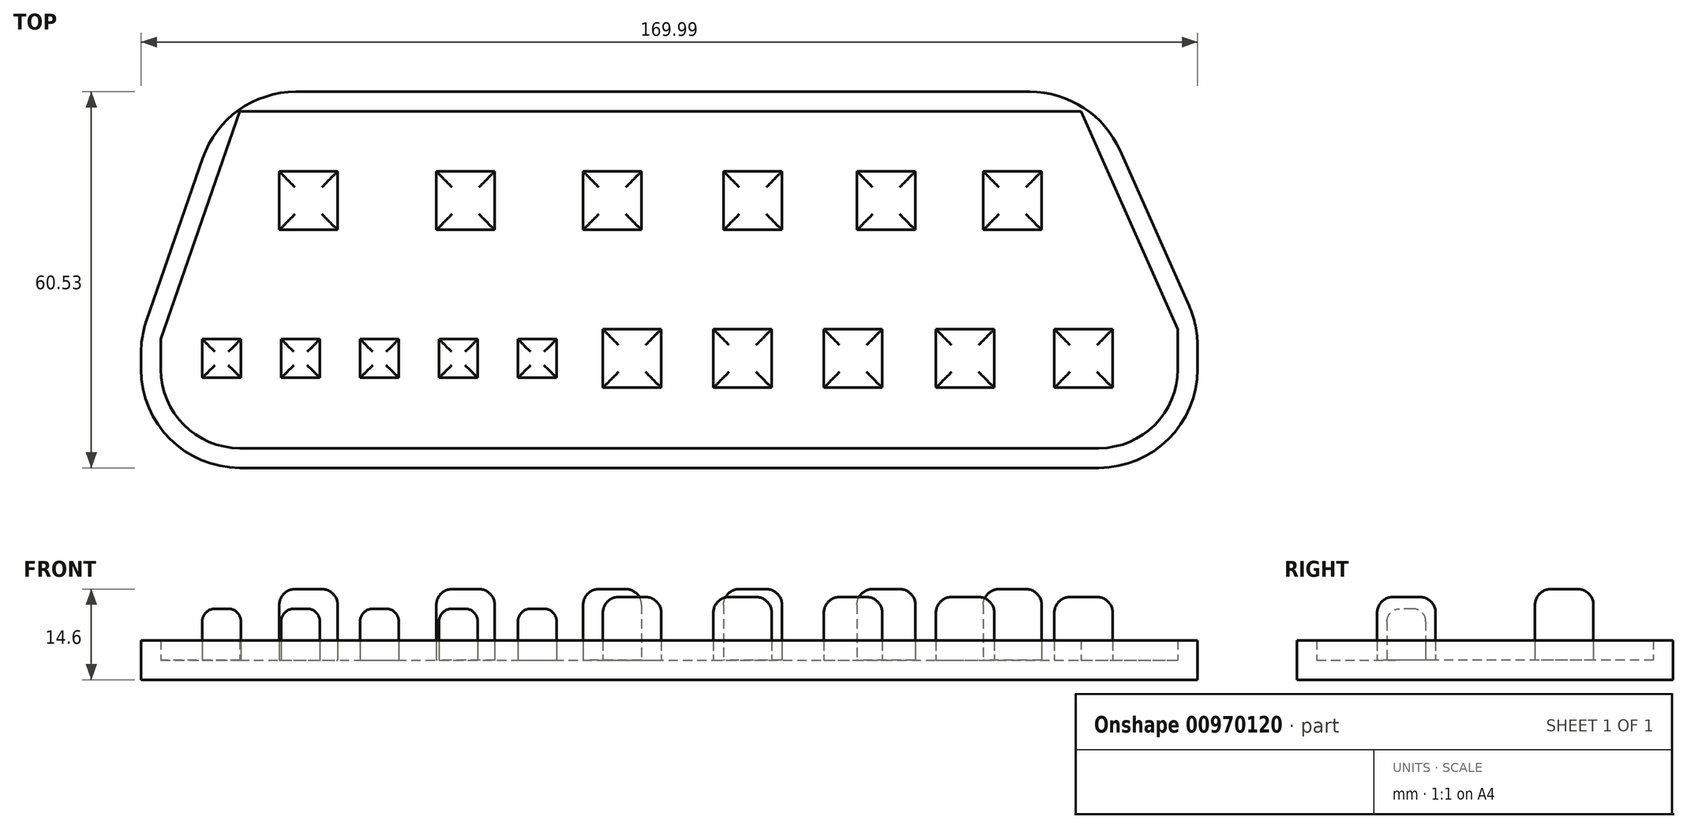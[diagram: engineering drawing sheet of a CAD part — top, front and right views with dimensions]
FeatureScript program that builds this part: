
annotation { "Feature Type Name" : "Feature", "Feature Type Description" : "" }
export const myFeature = defineFeature(function(context is Context, id is Id, definition is map)
    precondition{}
    {
        {
            var Q0;
            Q0=qCreatedBy(makeId("Top.planeOp"),FACE);
            var sketch = newSketch(context, id + "F0", { "sketchPlane" : qUnion([Q0])});
            skLineSegment(sketch, "E0.bottom", {"start": v(-9.72, 0.4) * mm, "end": v(153.92, 0.4) * mm});
            skLineSegment(sketch, "E0.top", {"start": v(-9.72, -53.77) * mm, "end": v(153.92, -53.77) * mm});
            skLineSegment(sketch, "E0.left", {"start": v(-9.72, 0.4) * mm, "end": v(-9.72, -53.77) * mm});
            skLineSegment(sketch, "E0.right", {"start": v(153.92, 0.4) * mm, "end": v(153.92, -53.77) * mm});
            skSolve(sketch);
        }
        {
            var Q0;
            Q0=makeQuery(id+"F0.imprint","IMPRINT",FACE,{"disambiguationData":[TD([[makeQuery(id+"F0.imprint","IMPRINT",EDGE,{"derivedFrom":sQuery(id+"F0.wireOp",EDGE,"E0.bottom")}),-1.0]])]});
            extrude(context, id + "F1", {"entities" : qUnion([Q0]), "oppositeDirection" : true, "depth" : 3.17 * mm, "offsetDistance" : 25.4 * mm});
        }
        {
            var Q0;
            Q0=qCreatedBy(makeId("Top.planeOp"),FACE);
            var sketch = newSketch(context, id + "F2", { "sketchPlane" : qUnion([Q0])});
            skLineSegment(sketch, "E1.bottom", {"start": v(9.33, -9.25) * mm, "end": v(18.73, -9.25) * mm});
            skLineSegment(sketch, "E1.top", {"start": v(9.33, -18.64) * mm, "end": v(18.73, -18.64) * mm});
            skLineSegment(sketch, "E1.left", {"start": v(9.33, -9.25) * mm, "end": v(9.33, -18.64) * mm});
            skLineSegment(sketch, "E1.right", {"start": v(18.73, -9.25) * mm, "end": v(18.73, -18.64) * mm});
            skLineSegment(sketch, "E2.bottom", {"start": v(44, -9.25) * mm, "end": v(34.6, -9.25) * mm});
            skLineSegment(sketch, "E2.top", {"start": v(44, -18.64) * mm, "end": v(34.6, -18.64) * mm});
            skLineSegment(sketch, "E2.left", {"start": v(44, -9.25) * mm, "end": v(44, -18.64) * mm});
            skLineSegment(sketch, "E3.bottom", {"start": v(67.63, -9.25) * mm, "end": v(58.23, -9.25) * mm});
            skLineSegment(sketch, "E3.top", {"start": v(67.63, -18.64) * mm, "end": v(58.23, -18.64) * mm});
            skLineSegment(sketch, "E3.left", {"start": v(67.63, -9.25) * mm, "end": v(67.63, -18.64) * mm});
            skLineSegment(sketch, "E3.right", {"start": v(58.23, -9.25) * mm, "end": v(58.23, -18.64) * mm});
            skLineSegment(sketch, "E4.bottom", {"start": v(90.23, -9.25) * mm, "end": v(80.84, -9.25) * mm});
            skLineSegment(sketch, "E4.top", {"start": v(90.23, -18.64) * mm, "end": v(80.84, -18.64) * mm});
            skLineSegment(sketch, "E4.left", {"start": v(90.23, -9.25) * mm, "end": v(90.23, -18.64) * mm});
            skLineSegment(sketch, "E4.right", {"start": v(80.84, -9.25) * mm, "end": v(80.84, -18.64) * mm});
            skLineSegment(sketch, "E5.bottom", {"start": v(111.7, -9.25) * mm, "end": v(102.3, -9.25) * mm});
            skLineSegment(sketch, "E5.top", {"start": v(111.7, -18.64) * mm, "end": v(102.3, -18.64) * mm});
            skLineSegment(sketch, "E5.left", {"start": v(111.7, -9.25) * mm, "end": v(111.7, -18.64) * mm});
            skLineSegment(sketch, "E5.right", {"start": v(102.3, -9.25) * mm, "end": v(102.3, -18.64) * mm});
            skLineSegment(sketch, "E6.bottom", {"start": v(132.02, -9.25) * mm, "end": v(122.62, -9.25) * mm});
            skLineSegment(sketch, "E6.top", {"start": v(132.02, -18.64) * mm, "end": v(122.62, -18.64) * mm});
            skLineSegment(sketch, "E6.left", {"start": v(132.02, -9.25) * mm, "end": v(132.02, -18.64) * mm});
            skLineSegment(sketch, "E6.right", {"start": v(122.62, -9.25) * mm, "end": v(122.62, -18.64) * mm});
            skLineSegment(sketch, "E7", {"start": v(34.6, -9.25) * mm, "end": v(34.6, -18.64) * mm});
            skSolve(sketch);
        }
        {
            var Q0;
            Q0=makeQuery(id+"F2.imprint","IMPRINT",FACE,{"disambiguationData":[TD([[makeQuery(id+"F2.imprint","IMPRINT",EDGE,{"derivedFrom":sQuery(id+"F2.wireOp",EDGE,"E1.bottom")}),-1.0]])]});
            var Q1;
            Q1=makeQuery(id+"F2.imprint","IMPRINT",FACE,{"disambiguationData":[TD([[makeQuery(id+"F2.imprint","IMPRINT",EDGE,{"derivedFrom":sQuery(id+"F2.wireOp",EDGE,"E2.bottom")}),1.0]])]});
            var Q2;
            Q2=makeQuery(id+"F2.imprint","IMPRINT",FACE,{"disambiguationData":[TD([[makeQuery(id+"F2.imprint","IMPRINT",EDGE,{"derivedFrom":sQuery(id+"F2.wireOp",EDGE,"E3.bottom")}),1.0]])]});
            var Q3;
            Q3=makeQuery(id+"F2.imprint","IMPRINT",FACE,{"disambiguationData":[TD([[makeQuery(id+"F2.imprint","IMPRINT",EDGE,{"derivedFrom":sQuery(id+"F2.wireOp",EDGE,"E4.bottom")}),1.0]])]});
            var Q4;
            Q4=makeQuery(id+"F2.imprint","IMPRINT",FACE,{"disambiguationData":[TD([[makeQuery(id+"F2.imprint","IMPRINT",EDGE,{"derivedFrom":sQuery(id+"F2.wireOp",EDGE,"E5.bottom")}),1.0]])]});
            var Q5;
            Q5=makeQuery(id+"F2.imprint","IMPRINT",FACE,{"disambiguationData":[TD([[makeQuery(id+"F2.imprint","IMPRINT",EDGE,{"derivedFrom":sQuery(id+"F2.wireOp",EDGE,"E6.bottom")}),1.0]])]});
            extrude(context, id + "F3", {"entities" : qUnion([Q0, Q1, Q2, Q3, Q4, Q5]), "operationType" : NewBodyOperationType.ADD, "depth" : 11.43 * mm, "offsetDistance" : 25.4 * mm});
        }
        {
            var Q0;
            Q0=makeQuery(id+"F1.opExtrude","CAP_FACE",FACE,{"disambiguationData":[OSD([sQuery(id+"F0.wireOp",EDGE,"E0.bottom"),sQuery(id+"F0.wireOp",EDGE,"E0.top"),sQuery(id+"F0.wireOp",EDGE,"E0.left"),sQuery(id+"F0.wireOp",EDGE,"E0.right")])],"isStart":true});
            var sketch = newSketch(context, id + "F4", { "sketchPlane" : qUnion([Q0])});
            skLineSegment(sketch, "E8", {"start": v(61.4, -34.65) * mm, "end": v(193.08, -34.65) * mm, "construction": true});
            skLineSegment(sketch, "E9.bottom", {"start": v(61.4, -34.65) * mm, "end": v(70.8, -34.65) * mm});
            skLineSegment(sketch, "E9.top", {"start": v(61.4, -44.04) * mm, "end": v(70.8, -44.04) * mm});
            skLineSegment(sketch, "E9.left", {"start": v(61.4, -34.65) * mm, "end": v(61.4, -44.04) * mm});
            skLineSegment(sketch, "E9.right", {"start": v(70.8, -34.65) * mm, "end": v(70.8, -44.04) * mm});
            skLineSegment(sketch, "E10.bottom", {"start": v(79.18, -34.65) * mm, "end": v(88.58, -34.65) * mm});
            skLineSegment(sketch, "E10.top", {"start": v(79.18, -44.04) * mm, "end": v(88.58, -44.04) * mm});
            skLineSegment(sketch, "E10.left", {"start": v(79.18, -34.65) * mm, "end": v(79.18, -44.04) * mm});
            skLineSegment(sketch, "E10.right", {"start": v(88.58, -34.65) * mm, "end": v(88.58, -44.04) * mm});
            skLineSegment(sketch, "E11.bottom", {"start": v(96.96, -34.65) * mm, "end": v(106.36, -34.65) * mm});
            skLineSegment(sketch, "E11.top", {"start": v(96.96, -44.04) * mm, "end": v(106.36, -44.04) * mm});
            skLineSegment(sketch, "E11.left", {"start": v(96.96, -34.65) * mm, "end": v(96.96, -44.04) * mm});
            skLineSegment(sketch, "E11.right", {"start": v(106.36, -34.65) * mm, "end": v(106.36, -44.04) * mm});
            skLineSegment(sketch, "E12.bottom", {"start": v(115, -34.65) * mm, "end": v(124.4, -34.65) * mm});
            skLineSegment(sketch, "E12.top", {"start": v(115, -44.04) * mm, "end": v(124.4, -44.04) * mm});
            skLineSegment(sketch, "E12.left", {"start": v(115, -34.65) * mm, "end": v(115, -44.04) * mm});
            skLineSegment(sketch, "E12.right", {"start": v(124.4, -34.65) * mm, "end": v(124.4, -44.04) * mm});
            skLineSegment(sketch, "E13.bottom", {"start": v(134.05, -34.65) * mm, "end": v(143.45, -34.65) * mm});
            skLineSegment(sketch, "E13.top", {"start": v(134.05, -44.04) * mm, "end": v(143.45, -44.04) * mm});
            skLineSegment(sketch, "E13.left", {"start": v(134.05, -34.65) * mm, "end": v(134.05, -44.04) * mm});
            skLineSegment(sketch, "E13.right", {"start": v(143.45, -34.65) * mm, "end": v(143.45, -44.04) * mm});
            skSolve(sketch);
        }
        {
            var Q0;
            Q0=makeQuery(id+"F4.imprint","IMPRINT",FACE,{"disambiguationData":[TD([[makeQuery(id+"F4.imprint","IMPRINT",EDGE,{"derivedFrom":sQuery(id+"F4.wireOp",EDGE,"E11.bottom")}),-1.0]])]});
            var Q1;
            Q1=makeQuery(id+"F4.imprint","IMPRINT",FACE,{"disambiguationData":[TD([[makeQuery(id+"F4.imprint","IMPRINT",EDGE,{"derivedFrom":sQuery(id+"F4.wireOp",EDGE,"E13.bottom")}),-1.0]])]});
            var Q2;
            Q2=makeQuery(id+"F4.imprint","IMPRINT",FACE,{"disambiguationData":[TD([[makeQuery(id+"F4.imprint","IMPRINT",EDGE,{"derivedFrom":sQuery(id+"F4.wireOp",EDGE,"E12.bottom")}),-1.0]])]});
            var Q3;
            Q3=makeQuery(id+"F4.imprint","IMPRINT",FACE,{"disambiguationData":[TD([[makeQuery(id+"F4.imprint","IMPRINT",EDGE,{"derivedFrom":sQuery(id+"F4.wireOp",EDGE,"E10.bottom")}),-1.0]])]});
            var Q4;
            Q4=makeQuery(id+"F4.imprint","IMPRINT",FACE,{"disambiguationData":[TD([[makeQuery(id+"F4.imprint","IMPRINT",EDGE,{"derivedFrom":sQuery(id+"F4.wireOp",EDGE,"E9.bottom")}),-1.0]])]});
            extrude(context, id + "F5", {"entities" : qUnion([Q0, Q1, Q2, Q3, Q4]), "operationType" : NewBodyOperationType.ADD, "depth" : 10.16 * mm, "offsetDistance" : 25.4 * mm});
        }
        {
            var Q0;
            Q0=makeQuery(id+"F3.opExtrude","CAP_FACE",FACE,{"disambiguationData":[OSD([sQuery(id+"F2.wireOp",EDGE,"E1.bottom"),sQuery(id+"F2.wireOp",EDGE,"E1.top"),sQuery(id+"F2.wireOp",EDGE,"E1.left"),sQuery(id+"F2.wireOp",EDGE,"E1.right")])],"isStart":false});
            var Q1;
            Q1=makeQuery(id+"F3.opExtrude","CAP_FACE",FACE,{"disambiguationData":[OSD([sQuery(id+"F2.wireOp",EDGE,"a6f74513-a6f5-46e5-be97-dc0fd28510d1.1.0.0"),sQuery(id+"F2.wireOp",EDGE,"a6f74513-a6f5-46e5-be97-dc0fd28510d1.1.0.1"),sQuery(id+"F2.wireOp",EDGE,"a6f74513-a6f5-46e5-be97-dc0fd28510d1.1.0.2"),sQuery(id+"F2.wireOp",EDGE,"a6f74513-a6f5-46e5-be97-dc0fd28510d1.1.0.3")])],"isStart":false});
            var Q2;
            Q2=makeQuery(id+"F3.opExtrude","CAP_FACE",FACE,{"disambiguationData":[OSD([sQuery(id+"F2.wireOp",EDGE,"a37b4573-0c43-4b9e-b34a-351aa36ba832.1.0.0"),sQuery(id+"F2.wireOp",EDGE,"a37b4573-0c43-4b9e-b34a-351aa36ba832.1.0.1"),sQuery(id+"F2.wireOp",EDGE,"a37b4573-0c43-4b9e-b34a-351aa36ba832.1.0.2"),sQuery(id+"F2.wireOp",EDGE,"a37b4573-0c43-4b9e-b34a-351aa36ba832.1.0.3")])],"isStart":false});
            var Q3;
            Q3=makeQuery(id+"F3.opExtrude","CAP_FACE",FACE,{"disambiguationData":[OSD([sQuery(id+"F2.wireOp",EDGE,"2544778d-07a4-4a01-85e0-11865cb4e7f5.1.0.0"),sQuery(id+"F2.wireOp",EDGE,"2544778d-07a4-4a01-85e0-11865cb4e7f5.1.0.2"),sQuery(id+"F2.wireOp",EDGE,"2544778d-07a4-4a01-85e0-11865cb4e7f5.1.0.3"),sQuery(id+"F2.wireOp",EDGE,"2544778d-07a4-4a01-85e0-11865cb4e7f5.1.0.4")])],"isStart":false});
            var Q4;
            Q4=makeQuery(id+"F3.opExtrude","CAP_FACE",FACE,{"disambiguationData":[OSD([sQuery(id+"F2.wireOp",EDGE,"e6729a68-15cc-43d3-9dee-f7c0bf543b0e.1.0.0"),sQuery(id+"F2.wireOp",EDGE,"e6729a68-15cc-43d3-9dee-f7c0bf543b0e.1.0.1"),sQuery(id+"F2.wireOp",EDGE,"e6729a68-15cc-43d3-9dee-f7c0bf543b0e.1.0.2"),sQuery(id+"F2.wireOp",EDGE,"e6729a68-15cc-43d3-9dee-f7c0bf543b0e.1.0.3")])],"isStart":false});
            var Q5;
            Q5=makeQuery(id+"F3.opExtrude","CAP_FACE",FACE,{"disambiguationData":[OSD([sQuery(id+"F2.wireOp",EDGE,"b651a250-4a59-4ffa-a352-21a7c59f4deb.1.0.0"),sQuery(id+"F2.wireOp",EDGE,"b651a250-4a59-4ffa-a352-21a7c59f4deb.1.0.1"),sQuery(id+"F2.wireOp",EDGE,"b651a250-4a59-4ffa-a352-21a7c59f4deb.1.0.2"),sQuery(id+"F2.wireOp",EDGE,"b651a250-4a59-4ffa-a352-21a7c59f4deb.1.0.3")])],"isStart":false});
            var Q6;
            Q6=makeQuery(id+"F3.opExtrude","CAP_FACE",FACE,{"disambiguationData":[OSD([sQuery(id+"F2.wireOp",EDGE,"60ef9c8b-74d5-4385-bd4f-73c425923557.1.0.0"),sQuery(id+"F2.wireOp",EDGE,"60ef9c8b-74d5-4385-bd4f-73c425923557.1.0.1"),sQuery(id+"F2.wireOp",EDGE,"60ef9c8b-74d5-4385-bd4f-73c425923557.1.0.2"),sQuery(id+"F2.wireOp",EDGE,"60ef9c8b-74d5-4385-bd4f-73c425923557.1.0.3")])],"isStart":false});
            var Q7;
            Q7=makeQuery(id+"F3.opExtrude","CAP_FACE",FACE,{"disambiguationData":[OSD([sQuery(id+"F2.wireOp",EDGE,"5298001d-e36e-4064-a5db-c45dce80e3df.1.0.1"),sQuery(id+"F2.wireOp",EDGE,"5298001d-e36e-4064-a5db-c45dce80e3df.1.0.2"),sQuery(id+"F2.wireOp",EDGE,"5298001d-e36e-4064-a5db-c45dce80e3df.1.0.3"),sQuery(id+"F2.wireOp",EDGE,"5298001d-e36e-4064-a5db-c45dce80e3df.1.0.4")])],"isStart":false});
            var Q8;
            Q8=makeQuery(id+"F3.opExtrude","CAP_FACE",FACE,{"disambiguationData":[OSD([sQuery(id+"F2.wireOp",EDGE,"E2.bottom"),sQuery(id+"F2.wireOp",EDGE,"E2.top"),sQuery(id+"F2.wireOp",EDGE,"E2.left"),sQuery(id+"F2.wireOp",EDGE,"E2.right")])],"isStart":false});
            var Q9;
            Q9=makeQuery(id+"F3.opExtrude","CAP_FACE",FACE,{"disambiguationData":[OSD([sQuery(id+"F2.wireOp",EDGE,"E3.bottom"),sQuery(id+"F2.wireOp",EDGE,"E3.top"),sQuery(id+"F2.wireOp",EDGE,"E3.left"),sQuery(id+"F2.wireOp",EDGE,"E3.right")])],"isStart":false});
            var Q10;
            Q10=makeQuery(id+"F3.opExtrude","CAP_FACE",FACE,{"disambiguationData":[OSD([sQuery(id+"F2.wireOp",EDGE,"E4.bottom"),sQuery(id+"F2.wireOp",EDGE,"E4.top"),sQuery(id+"F2.wireOp",EDGE,"E4.left"),sQuery(id+"F2.wireOp",EDGE,"E4.right")])],"isStart":false});
            var Q11;
            Q11=makeQuery(id+"F3.opExtrude","CAP_FACE",FACE,{"disambiguationData":[OSD([sQuery(id+"F2.wireOp",EDGE,"E5.bottom"),sQuery(id+"F2.wireOp",EDGE,"E5.top"),sQuery(id+"F2.wireOp",EDGE,"E5.left"),sQuery(id+"F2.wireOp",EDGE,"E5.right")])],"isStart":false});
            var Q12;
            Q12=makeQuery(id+"F3.opExtrude","CAP_FACE",FACE,{"disambiguationData":[OSD([sQuery(id+"F2.wireOp",EDGE,"E6.bottom"),sQuery(id+"F2.wireOp",EDGE,"E6.top"),sQuery(id+"F2.wireOp",EDGE,"E6.left"),sQuery(id+"F2.wireOp",EDGE,"E6.right")])],"isStart":false});
            fillet(context, id + "F6", {"entities" : qUnion([Q0, Q1, Q2, Q3, Q4, Q5, Q6, Q7, Q8, Q9, Q10, Q11, Q12]), "radius" : 2.54 * mm, "tangentPropagation" : true, "allowEdgeOverflow" : false});
        }
        {
            var Q0;
            Q0=makeQuery(id+"F5.opExtrude","CAP_FACE",FACE,{"disambiguationData":[OSD([sQuery(id+"F4.wireOp",EDGE,"E9.bottom"),sQuery(id+"F4.wireOp",EDGE,"E9.top"),sQuery(id+"F4.wireOp",EDGE,"E9.left"),sQuery(id+"F4.wireOp",EDGE,"E9.right")])],"isStart":false});
            var Q1;
            Q1=makeQuery(id+"F5.opExtrude","CAP_FACE",FACE,{"disambiguationData":[OSD([sQuery(id+"F4.wireOp",EDGE,"E10.bottom"),sQuery(id+"F4.wireOp",EDGE,"E10.top"),sQuery(id+"F4.wireOp",EDGE,"E10.left"),sQuery(id+"F4.wireOp",EDGE,"E10.right")])],"isStart":false});
            var Q2;
            Q2=makeQuery(id+"F5.opExtrude","CAP_FACE",FACE,{"disambiguationData":[OSD([sQuery(id+"F4.wireOp",EDGE,"E11.bottom"),sQuery(id+"F4.wireOp",EDGE,"E11.top"),sQuery(id+"F4.wireOp",EDGE,"E11.left"),sQuery(id+"F4.wireOp",EDGE,"E11.right")])],"isStart":false});
            var Q3;
            Q3=makeQuery(id+"F5.opExtrude","CAP_FACE",FACE,{"disambiguationData":[OSD([sQuery(id+"F4.wireOp",EDGE,"E12.bottom"),sQuery(id+"F4.wireOp",EDGE,"E12.top"),sQuery(id+"F4.wireOp",EDGE,"E12.left"),sQuery(id+"F4.wireOp",EDGE,"E12.right")])],"isStart":false});
            var Q4;
            Q4=makeQuery(id+"F5.opExtrude","CAP_FACE",FACE,{"disambiguationData":[OSD([sQuery(id+"F4.wireOp",EDGE,"E13.bottom"),sQuery(id+"F4.wireOp",EDGE,"E13.top"),sQuery(id+"F4.wireOp",EDGE,"E13.left"),sQuery(id+"F4.wireOp",EDGE,"E13.right")])],"isStart":false});
            var Q5;
            Q5=makeQuery(id+"F5.opExtrude","CAP_FACE",FACE,{"disambiguationData":[OSD([sQuery(id+"F4.wireOp",EDGE,"HuPphu0x-Gtiq-LhBo-5UTa-TvdvrvVJAFvw.bottom"),sQuery(id+"F4.wireOp",EDGE,"HuPphu0x-Gtiq-LhBo-5UTa-TvdvrvVJAFvw.top"),sQuery(id+"F4.wireOp",EDGE,"HuPphu0x-Gtiq-LhBo-5UTa-TvdvrvVJAFvw.left"),sQuery(id+"F4.wireOp",EDGE,"HuPphu0x-Gtiq-LhBo-5UTa-TvdvrvVJAFvw.right")])],"isStart":false});
            var Q6;
            Q6=makeQuery(id+"F5.opExtrude","CAP_FACE",FACE,{"disambiguationData":[OSD([sQuery(id+"F4.wireOp",EDGE,"e8lRvLqR-yIOs-Yckj-3nDI-QBPCZNJgAbyx.bottom"),sQuery(id+"F4.wireOp",EDGE,"e8lRvLqR-yIOs-Yckj-3nDI-QBPCZNJgAbyx.top"),sQuery(id+"F4.wireOp",EDGE,"e8lRvLqR-yIOs-Yckj-3nDI-QBPCZNJgAbyx.left"),sQuery(id+"F4.wireOp",EDGE,"e8lRvLqR-yIOs-Yckj-3nDI-QBPCZNJgAbyx.right")])],"isStart":false});
            var Q7;
            Q7=makeQuery(id+"F5.opExtrude","CAP_FACE",FACE,{"disambiguationData":[OSD([sQuery(id+"F4.wireOp",EDGE,"93dc5489-29b0-42f7-b222-2c44c2208c07.1.0.0"),sQuery(id+"F4.wireOp",EDGE,"93dc5489-29b0-42f7-b222-2c44c2208c07.1.0.1"),sQuery(id+"F4.wireOp",EDGE,"93dc5489-29b0-42f7-b222-2c44c2208c07.1.0.2"),sQuery(id+"F4.wireOp",EDGE,"93dc5489-29b0-42f7-b222-2c44c2208c07.1.0.3")])],"isStart":false});
            fillet(context, id + "F7", {"entities" : qUnion([Q0, Q1, Q2, Q3, Q4, Q5, Q6, Q7]), "radius" : 2.54 * mm, "tangentPropagation" : true, "allowEdgeOverflow" : false});
        }
        {
            var Q0;
            Q0=makeQuery(id+"F1.opExtrude","CAP_FACE",FACE,{"disambiguationData":[OSD([sQuery(id+"F0.wireOp",EDGE,"E0.bottom"),sQuery(id+"F0.wireOp",EDGE,"E0.top"),sQuery(id+"F0.wireOp",EDGE,"E0.left"),sQuery(id+"F0.wireOp",EDGE,"E0.right")])],"isStart":true});
            var sketch = newSketch(context, id + "F8", { "sketchPlane" : qUnion([Q0])});
            skLineSegment(sketch, "E14", {"start": v(113.95, -36.23) * mm, "end": v(235.74, -36.23) * mm, "construction": true});
            skLineSegment(sketch, "E15.bottom", {"start": v(47.75, -36.23) * mm, "end": v(53.98, -36.23) * mm});
            skLineSegment(sketch, "E15.top", {"start": v(47.75, -42.46) * mm, "end": v(53.98, -42.46) * mm});
            skLineSegment(sketch, "E15.left", {"start": v(47.75, -36.23) * mm, "end": v(47.75, -42.46) * mm});
            skLineSegment(sketch, "E15.right", {"start": v(53.98, -36.23) * mm, "end": v(53.98, -42.46) * mm});
            skLineSegment(sketch, "E16.1.0.0", {"start": v(41.28, -36.23) * mm, "end": v(41.28, -42.46) * mm});
            skLineSegment(sketch, "E16.1.0.1", {"start": v(35.05, -36.23) * mm, "end": v(41.28, -36.23) * mm});
            skLineSegment(sketch, "E16.1.0.2", {"start": v(35.05, -36.23) * mm, "end": v(35.05, -42.46) * mm});
            skLineSegment(sketch, "E16.1.0.3", {"start": v(35.05, -42.46) * mm, "end": v(41.28, -42.46) * mm});
            skLineSegment(sketch, "E16.2.0.0", {"start": v(28.58, -36.23) * mm, "end": v(28.58, -42.46) * mm});
            skLineSegment(sketch, "E16.2.0.1", {"start": v(22.35, -36.23) * mm, "end": v(28.58, -36.23) * mm});
            skLineSegment(sketch, "E16.2.0.2", {"start": v(22.35, -36.23) * mm, "end": v(22.35, -42.46) * mm});
            skLineSegment(sketch, "E16.2.0.3", {"start": v(22.35, -42.46) * mm, "end": v(28.58, -42.46) * mm});
            skLineSegment(sketch, "E16.3.0.0", {"start": v(15.88, -36.23) * mm, "end": v(15.88, -42.46) * mm});
            skLineSegment(sketch, "E16.3.0.1", {"start": v(9.65, -36.23) * mm, "end": v(15.88, -36.23) * mm});
            skLineSegment(sketch, "E16.3.0.2", {"start": v(9.65, -36.23) * mm, "end": v(9.65, -42.46) * mm});
            skLineSegment(sketch, "E16.3.0.3", {"start": v(9.65, -42.46) * mm, "end": v(15.88, -42.46) * mm});
            skLineSegment(sketch, "E16.4.0.0", {"start": v(3.17, -36.23) * mm, "end": v(3.17, -42.46) * mm});
            skLineSegment(sketch, "E16.4.0.1", {"start": v(-3.05, -36.23) * mm, "end": v(3.17, -36.23) * mm});
            skLineSegment(sketch, "E16.4.0.2", {"start": v(-3.05, -36.23) * mm, "end": v(-3.05, -42.46) * mm});
            skLineSegment(sketch, "E16.4.0.3", {"start": v(-3.05, -42.46) * mm, "end": v(3.17, -42.46) * mm});
            skLineSegment(sketch, "E16.direction1", {"start": v(47.75, -42.46) * mm, "end": v(35.05, -42.46) * mm, "construction": true});
            skSolve(sketch);
        }
        {
            var Q0;
            Q0=makeQuery(id+"F8.imprint","IMPRINT",FACE,{"disambiguationData":[TD([[makeQuery(id+"F8.imprint","IMPRINT",EDGE,{"derivedFrom":sQuery(id+"F8.wireOp",EDGE,"E15.bottom")}),-1.0]])]});
            var Q1;
            Q1=makeQuery(id+"F8.imprint","IMPRINT",FACE,{"disambiguationData":[TD([[makeQuery(id+"F8.imprint","IMPRINT",EDGE,{"derivedFrom":sQuery(id+"F8.wireOp",EDGE,"E16.1.0.0")}),-1.0]])]});
            var Q2;
            Q2=makeQuery(id+"F8.imprint","IMPRINT",FACE,{"disambiguationData":[TD([[makeQuery(id+"F8.imprint","IMPRINT",EDGE,{"derivedFrom":sQuery(id+"F8.wireOp",EDGE,"E16.2.0.0")}),-1.0]])]});
            var Q3;
            Q3=makeQuery(id+"F8.imprint","IMPRINT",FACE,{"disambiguationData":[TD([[makeQuery(id+"F8.imprint","IMPRINT",EDGE,{"derivedFrom":sQuery(id+"F8.wireOp",EDGE,"E16.3.0.0")}),-1.0]])]});
            var Q4;
            Q4=makeQuery(id+"F8.imprint","IMPRINT",FACE,{"disambiguationData":[TD([[makeQuery(id+"F8.imprint","IMPRINT",EDGE,{"derivedFrom":sQuery(id+"F8.wireOp",EDGE,"E16.4.0.0")}),-1.0]])]});
            var Q5;
            Q5=sQuery(id+"F8.wireOp",EDGE,"A3gFyePg-5LmW-fe9U-Uoda-R7NkxVjHE0qn.left");
            var Q6;
            Q6=sQuery(id+"F8.wireOp",EDGE,"A3gFyePg-5LmW-fe9U-Uoda-R7NkxVjHE0qn.bottom");
            var Q7;
            Q7=sQuery(id+"F8.wireOp",EDGE,"A3gFyePg-5LmW-fe9U-Uoda-R7NkxVjHE0qn.right");
            var Q8;
            Q8=sQuery(id+"F8.wireOp",EDGE,"A3gFyePg-5LmW-fe9U-Uoda-R7NkxVjHE0qn.top");
            extrude(context, id + "F9", {"entities" : qUnion([Q0, Q1, Q2, Q3, Q4]), "operationType" : NewBodyOperationType.ADD, "surfaceEntities" : qUnion([Q5, Q6, Q7, Q8]), "depth" : 8.25 * mm, "offsetDistance" : 25.4 * mm});
        }
        {
            var Q0;
            Q0=makeQuery(id+"F9.opExtrude","CAP_FACE",FACE,{"disambiguationData":[OSD([sQuery(id+"F8.wireOp",EDGE,"E15.bottom"),sQuery(id+"F8.wireOp",EDGE,"E15.top"),sQuery(id+"F8.wireOp",EDGE,"E15.left"),sQuery(id+"F8.wireOp",EDGE,"E15.right")])],"isStart":false});
            var Q1;
            Q1=makeQuery(id+"F9.opExtrude","CAP_FACE",FACE,{"disambiguationData":[OSD([sQuery(id+"F8.wireOp",EDGE,"E16.1.0.0"),sQuery(id+"F8.wireOp",EDGE,"E16.1.0.1"),sQuery(id+"F8.wireOp",EDGE,"E16.1.0.2"),sQuery(id+"F8.wireOp",EDGE,"E16.1.0.3")])],"isStart":false});
            var Q2;
            Q2=makeQuery(id+"F9.opExtrude","CAP_FACE",FACE,{"disambiguationData":[OSD([sQuery(id+"F8.wireOp",EDGE,"E16.2.0.0"),sQuery(id+"F8.wireOp",EDGE,"E16.2.0.1"),sQuery(id+"F8.wireOp",EDGE,"E16.2.0.2"),sQuery(id+"F8.wireOp",EDGE,"E16.2.0.3")])],"isStart":false});
            var Q3;
            Q3=makeQuery(id+"F9.opExtrude","CAP_FACE",FACE,{"disambiguationData":[OSD([sQuery(id+"F8.wireOp",EDGE,"E16.3.0.0"),sQuery(id+"F8.wireOp",EDGE,"E16.3.0.1"),sQuery(id+"F8.wireOp",EDGE,"E16.3.0.2"),sQuery(id+"F8.wireOp",EDGE,"E16.3.0.3")])],"isStart":false});
            var Q4;
            Q4=makeQuery(id+"F9.opExtrude","CAP_FACE",FACE,{"disambiguationData":[OSD([sQuery(id+"F8.wireOp",EDGE,"E16.4.0.0"),sQuery(id+"F8.wireOp",EDGE,"E16.4.0.1"),sQuery(id+"F8.wireOp",EDGE,"E16.4.0.2"),sQuery(id+"F8.wireOp",EDGE,"E16.4.0.3")])],"isStart":false});
            fillet(context, id + "F10", {"entities" : qUnion([Q0, Q1, Q2, Q3, Q4]), "radius" : 2.03 * mm, "tangentPropagation" : true, "allowEdgeOverflow" : false});
        }
        {
            var Q0;
            Q0=makeQuery(id+"F1.opExtrude","CAP_FACE",FACE,{"disambiguationData":[OSD([sQuery(id+"F0.wireOp",EDGE,"E0.bottom"),sQuery(id+"F0.wireOp",EDGE,"E0.top"),sQuery(id+"F0.wireOp",EDGE,"E0.left"),sQuery(id+"F0.wireOp",EDGE,"E0.right")])],"isStart":true});
            var sketch = newSketch(context, id + "F11", { "sketchPlane" : qUnion([Q0])});
            skLineSegment(sketch, "E17", {"start": v(2.98, 0.4) * mm, "end": v(-9.72, -36.23) * mm});
            skLineSegment(sketch, "E18", {"start": v(138.37, 0.4) * mm, "end": v(153.92, -34.65) * mm});
            skPoint(sketch, "E19", {"position": v(132.02, -13.94) * mm});
            skLineSegment(sketch, "E20", {"start": v(2.98, 0.4) * mm, "end": v(-15.36, 6.28) * mm});
            skLineSegment(sketch, "E21", {"start": v(-15.36, 6.28) * mm, "end": v(-9.72, -36.23) * mm});
            skLineSegment(sketch, "E22", {"start": v(138.37, 0.4) * mm, "end": v(160.94, 5.67) * mm});
            skLineSegment(sketch, "E23", {"start": v(160.94, 5.67) * mm, "end": v(153.92, -34.65) * mm});
            skSolve(sketch);
        }
        {
            var Q0;
            Q0 = qSketchRegion(id + "F11", true);
            extrude(context, id + "F12", {"entities" : qUnion([Q0]), "operationType" : NewBodyOperationType.REMOVE, "oppositeDirection" : true, "depth" : 25.4 * mm, "offsetDistance" : 25.4 * mm});
        }
        {
            var Q0;
            Q0=makeQuery(id+"F12.boolean.opBoolean","COPY",EDGE,{"derivedFrom":makeQuery(id+"F12.opExtrude","SWEPT_EDGE",EDGE,{"disambiguationData":[OSD([sQuery(id+"F0.wireOp",EDGE,"E0.bottom"),sQuery(id+"F11.wireOp",EDGE,"E17"),sQuery(id+"F11.wireOp",EDGE,"E20")])]})});
            var Q1;
            Q1=makeQuery(id+"F12.boolean.opBoolean","COPY",EDGE,{"derivedFrom":makeQuery(id+"F12.opExtrude","SWEPT_EDGE",EDGE,{"disambiguationData":[OSD([sQuery(id+"F0.wireOp",EDGE,"E0.left"),sQuery(id+"F11.wireOp",EDGE,"E17"),sQuery(id+"F11.wireOp",EDGE,"E21")])]})});
            var Q2;
            Q2=makeQuery(id+"F1.opExtrude","SWEPT_EDGE",EDGE,{"disambiguationData":[OSD([sQuery(id+"F0.wireOp",EDGE,"E0.top"),sQuery(id+"F0.wireOp",EDGE,"E0.left")])]});
            var Q3;
            Q3=makeQuery(id+"F1.opExtrude","SWEPT_EDGE",EDGE,{"disambiguationData":[OSD([sQuery(id+"F0.wireOp",EDGE,"E0.top"),sQuery(id+"F0.wireOp",EDGE,"E0.right")])]});
            var Q4;
            Q4=makeQuery(id+"F12.boolean.opBoolean","COPY",EDGE,{"derivedFrom":makeQuery(id+"F12.opExtrude","SWEPT_EDGE",EDGE,{"disambiguationData":[OSD([sQuery(id+"F0.wireOp",EDGE,"E0.right"),sQuery(id+"F11.wireOp",EDGE,"E18"),sQuery(id+"F11.wireOp",EDGE,"E23")])]})});
            var Q5;
            Q5=makeQuery(id+"F12.boolean.opBoolean","COPY",EDGE,{"derivedFrom":makeQuery(id+"F12.opExtrude","SWEPT_EDGE",EDGE,{"disambiguationData":[OSD([sQuery(id+"F0.wireOp",EDGE,"E0.bottom"),sQuery(id+"F11.wireOp",EDGE,"E18"),sQuery(id+"F11.wireOp",EDGE,"E22")])]})});
            fillet(context, id + "F13", {"entities" : qUnion([Q0, Q1, Q2, Q3, Q4, Q5]), "radius" : 12.7 * mm, "tangentPropagation" : true, "allowEdgeOverflow" : false});
        }
        {
            var Q0;
            Q0=makeQuery(id+"F1.opExtrude","CAP_FACE",FACE,{"disambiguationData":[OSD([sQuery(id+"F0.wireOp",EDGE,"E0.bottom"),sQuery(id+"F0.wireOp",EDGE,"E0.top"),sQuery(id+"F0.wireOp",EDGE,"E0.left"),sQuery(id+"F0.wireOp",EDGE,"E0.right")])],"isStart":false});
            var sketch = newSketch(context, id + "F14", { "sketchPlane" : qUnion([Q0])});
            skLineSegment(sketch, "E24.0", {"start": v(2.98, 56.95) * mm, "end": v(141.22, 56.95) * mm});
            skArc(sketch, "E24.1", {"start": v(-2.98, 7.1) * mm, "mid": v(2.82, -0.64) * mm, "end": v(12.02, -3.58) * mm});
            skLineSegment(sketch, "E24.2", {"start": v(-2.98, 7.1) * mm, "end": v(-12.01, 33.17) * mm});
            skArc(sketch, "E24.3", {"start": v(-12.9, 38.37) * mm, "mid": v(-12.67, 35.74) * mm, "end": v(-12.01, 33.17) * mm});
            skLineSegment(sketch, "E24.4", {"start": v(-12.9, 38.37) * mm, "end": v(-12.9, 41.07) * mm});
            skLineSegment(sketch, "E24.5", {"start": v(12.02, -3.58) * mm, "end": v(130.1, -3.58) * mm});
            skArc(sketch, "E24.6", {"start": v(2.98, 56.95) * mm, "mid": v(-8.24, 52.3) * mm, "end": v(-12.9, 41.07) * mm});
            skArc(sketch, "E24.7", {"start": v(130.1, -3.58) * mm, "mid": v(138.76, -1.02) * mm, "end": v(144.62, 5.85) * mm});
            skLineSegment(sketch, "E24.8", {"start": v(144.62, 5.85) * mm, "end": v(155.73, 30.9) * mm});
            skArc(sketch, "E24.9", {"start": v(155.73, 30.9) * mm, "mid": v(156.75, 34.05) * mm, "end": v(157.1, 37.34) * mm});
            skLineSegment(sketch, "E24.10", {"start": v(157.1, 37.34) * mm, "end": v(157.1, 41.07) * mm});
            skArc(sketch, "E24.11", {"start": v(157.1, 41.07) * mm, "mid": v(152.45, 52.3) * mm, "end": v(141.22, 56.95) * mm});
            skSolve(sketch);
        }
        {
            var Q0;
            Q0=makeQuery(id+"F14.imprint","IMPRINT",FACE,{"disambiguationData":[TD([[makeQuery(id+"F14.imprint","IMPRINT",EDGE,{"derivedFrom":sQuery(id+"F14.wireOp",EDGE,"E24.0")}),-1.0]])]});
            extrude(context, id + "F15", {"entities" : qUnion([Q0]), "operationType" : NewBodyOperationType.ADD, "oppositeDirection" : true, "depth" : 6.35 * mm, "offsetDistance" : 25.4 * mm});
        }
    });
